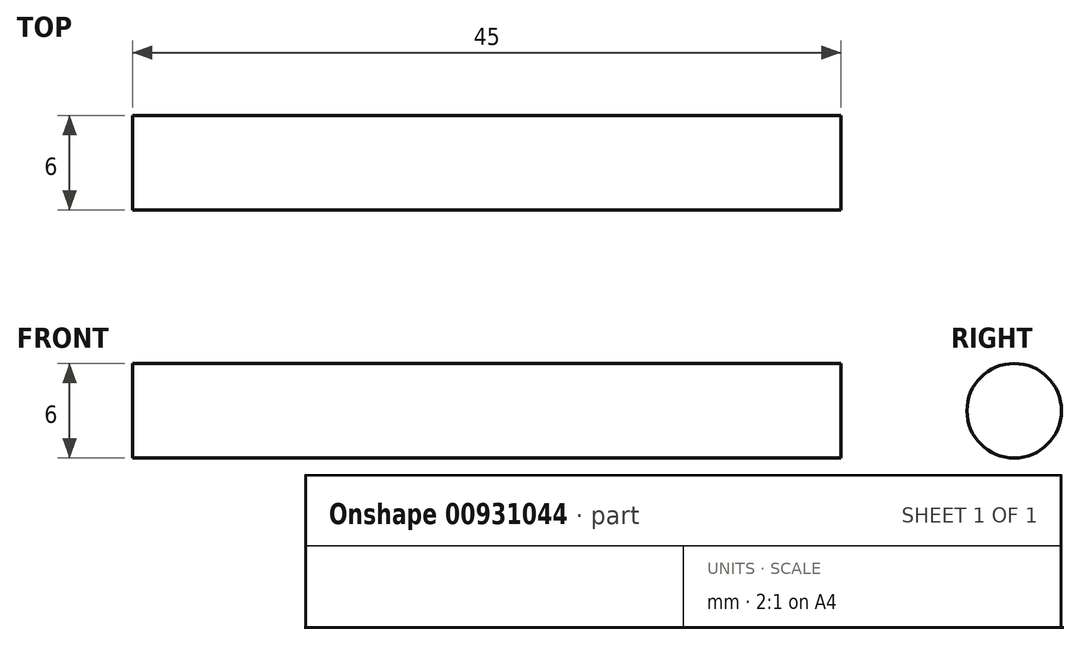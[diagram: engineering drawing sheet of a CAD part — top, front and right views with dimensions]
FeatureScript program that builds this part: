
annotation { "Feature Type Name" : "Feature", "Feature Type Description" : "" }
export const myFeature = defineFeature(function(context is Context, id is Id, definition is map)
    precondition{}
    {
        {
            var Q0;
            Q0=qCreatedBy(makeId("Right.planeOp"),FACE);
            var sketch = newSketch(context, id + "F0", { "sketchPlane" : qUnion([Q0])});
            skCircle(sketch, "E0", {"center": v(0, 0) * mm, "radius": 3 * mm});
            skSolve(sketch);
        }
        {
            var Q0;
            Q0=makeQuery(id+"F0.imprint","IMPRINT",FACE,{"disambiguationData":[TD([[makeQuery(id+"F0.imprint","IMPRINT",EDGE,{"derivedFrom":sQuery(id+"F0.wireOp",EDGE,"E0")}),1.0]])]});
            extrude(context, id + "F1", {"entities" : qUnion([Q0]), "depth" : 45 * mm, "offsetDistance" : 25 * mm, "symmetric" : true});
        }
    });
